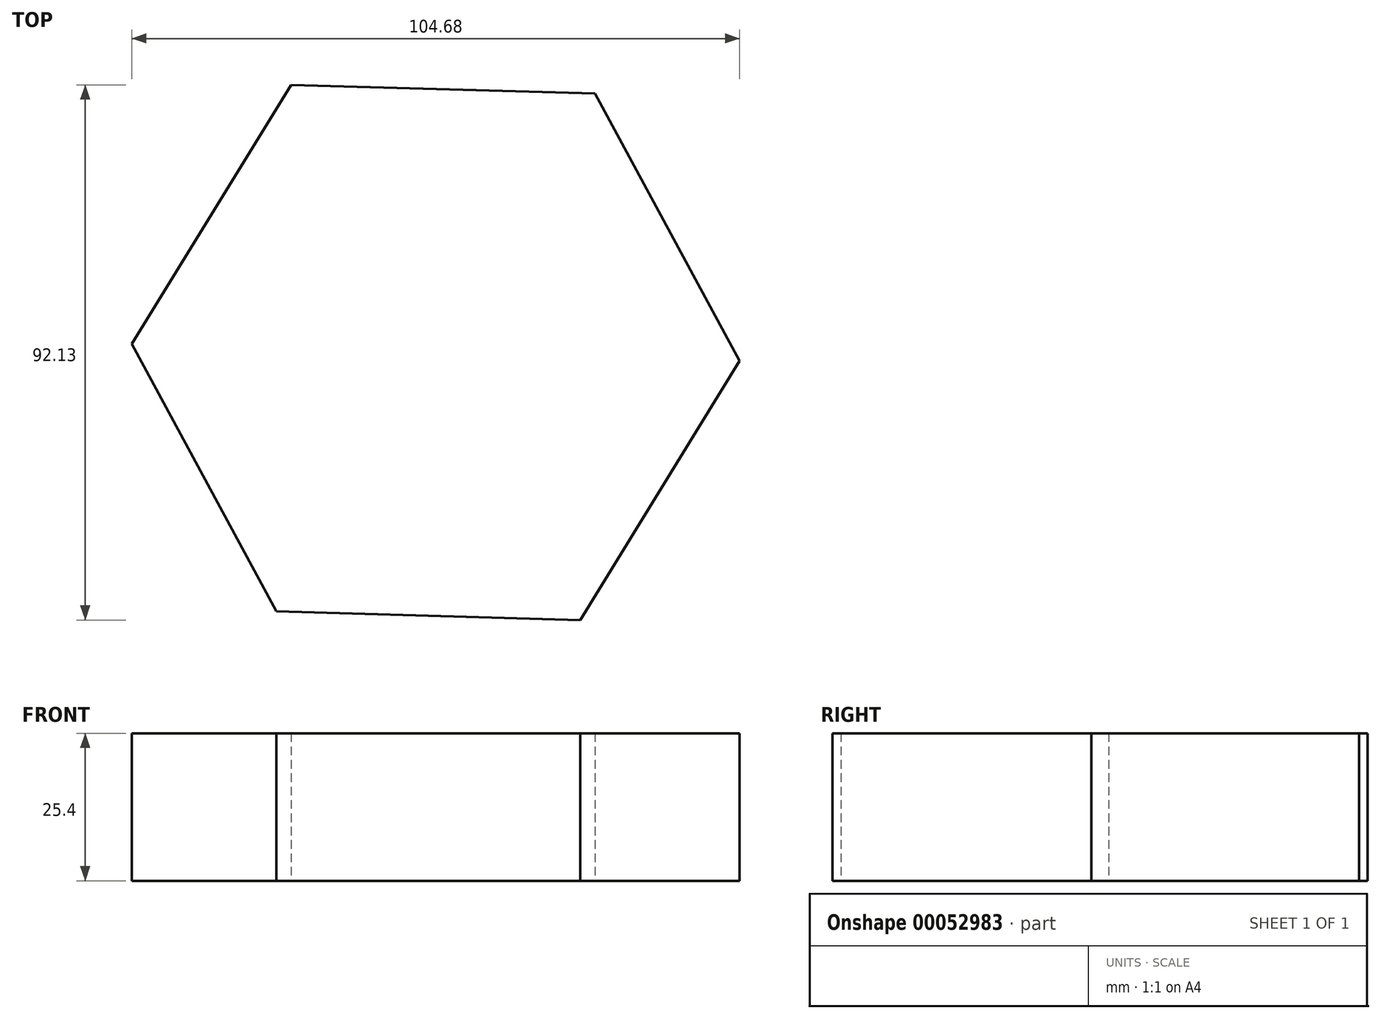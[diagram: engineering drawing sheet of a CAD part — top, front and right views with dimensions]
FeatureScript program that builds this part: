
annotation { "Feature Type Name" : "Feature", "Feature Type Description" : "" }
export const myFeature = defineFeature(function(context is Context, id is Id, definition is map)
    precondition{}
    {
        {
            var Q0;
            Q0=qCreatedBy(makeId("Top.planeOp"),FACE);
            var sketch = newSketch(context, id + "F0", { "sketchPlane" : qUnion([Q0])});
            skCircle(sketch, "E0.cCircle", {"center": v(-65.74, 57.52) * mm, "radius": 46.49 * mm, "construction": true});
            skLineSegment(sketch, "E0.0", {"start": v(-38.9, 104) * mm, "end": v(-12.07, 57.5) * mm});
            skLineSegment(sketch, "E0.1", {"start": v(-12.07, 57.5) * mm, "end": v(-38.92, 11.03) * mm});
            skLineSegment(sketch, "E0.2", {"start": v(-38.92, 11.03) * mm, "end": v(-92.6, 11.04) * mm});
            skLineSegment(sketch, "E0.3", {"start": v(-92.6, 11.04) * mm, "end": v(-119.42, 57.53) * mm});
            skLineSegment(sketch, "E0.4", {"start": v(-119.42, 57.53) * mm, "end": v(-92.57, 104) * mm});
            skLineSegment(sketch, "E0.5", {"start": v(-92.57, 104) * mm, "end": v(-38.9, 104) * mm});
            skPoint(sketch, "E0.0.midPoint", {"position": v(-25.48, 80.75) * mm});
            skSolve(sketch);
        }
        {
            var Q0;
            Q0 = qSketchRegion(id + "F0", true);
            var Q1;
            Q1=sQuery(id+"F0.wireOp",EDGE,"E0.2");
            var Q2;
            Q2=sQuery(id+"F0.wireOp",EDGE,"E0.1");
            var Q3;
            Q3=sQuery(id+"F0.wireOp",EDGE,"E0.3");
            var Q4;
            Q4=sQuery(id+"F0.wireOp",EDGE,"E0.4");
            var Q5;
            Q5=sQuery(id+"F0.wireOp",EDGE,"E0.5");
            var Q6;
            Q6=sQuery(id+"F0.wireOp",EDGE,"E0.0");
            extrude(context, id + "F1", {"entities" : qUnion([Q0]), "bodyType" : ToolBodyType.SURFACE, "operationType" : NewBodyOperationType.ADD, "surfaceEntities" : qUnion([Q1, Q2, Q3, Q4, Q5, Q6]), "depth" : 108.28 * mm});
        }
        {
            var Q0;
            Q0=makeQuery(id+"F0.imprint","IMPRINT",FACE,{"disambiguationData":[TD([[makeQuery(id+"F0.imprint","IMPRINT",EDGE,{"derivedFrom":sQuery(id+"F0.wireOp",EDGE,"E0.0")}),-1.0]])]});
            var sketch = newSketch(context, id + "F2", { "sketchPlane" : qUnion([Q0])});
            skCircle(sketch, "E1.cCircle", {"center": v(-66.14, 57.52) * mm, "radius": 45.35 * mm, "construction": true});
            skLineSegment(sketch, "E1.0", {"start": v(-118.48, 59) * mm, "end": v(-91.04, 103.59) * mm});
            skLineSegment(sketch, "E1.1", {"start": v(-91.04, 103.59) * mm, "end": v(-38.7, 102.11) * mm});
            skLineSegment(sketch, "E1.2", {"start": v(-38.7, 102.11) * mm, "end": v(-13.8, 56.05) * mm});
            skLineSegment(sketch, "E1.3", {"start": v(-13.8, 56.05) * mm, "end": v(-41.25, 11.46) * mm});
            skLineSegment(sketch, "E1.4", {"start": v(-41.25, 11.46) * mm, "end": v(-93.6, 12.93) * mm});
            skLineSegment(sketch, "E1.5", {"start": v(-93.6, 12.93) * mm, "end": v(-118.48, 59) * mm});
            skPoint(sketch, "E1.0.midPoint", {"position": v(-104.76, 81.3) * mm});
            skSolve(sketch);
        }
        {
            var Q0;
            Q0 = qSketchRegion(id + "F2", true);
            extrude(context, id + "F3", {"entities" : qUnion([Q0]), "depth" : 25.4 * mm});
        }
    });
